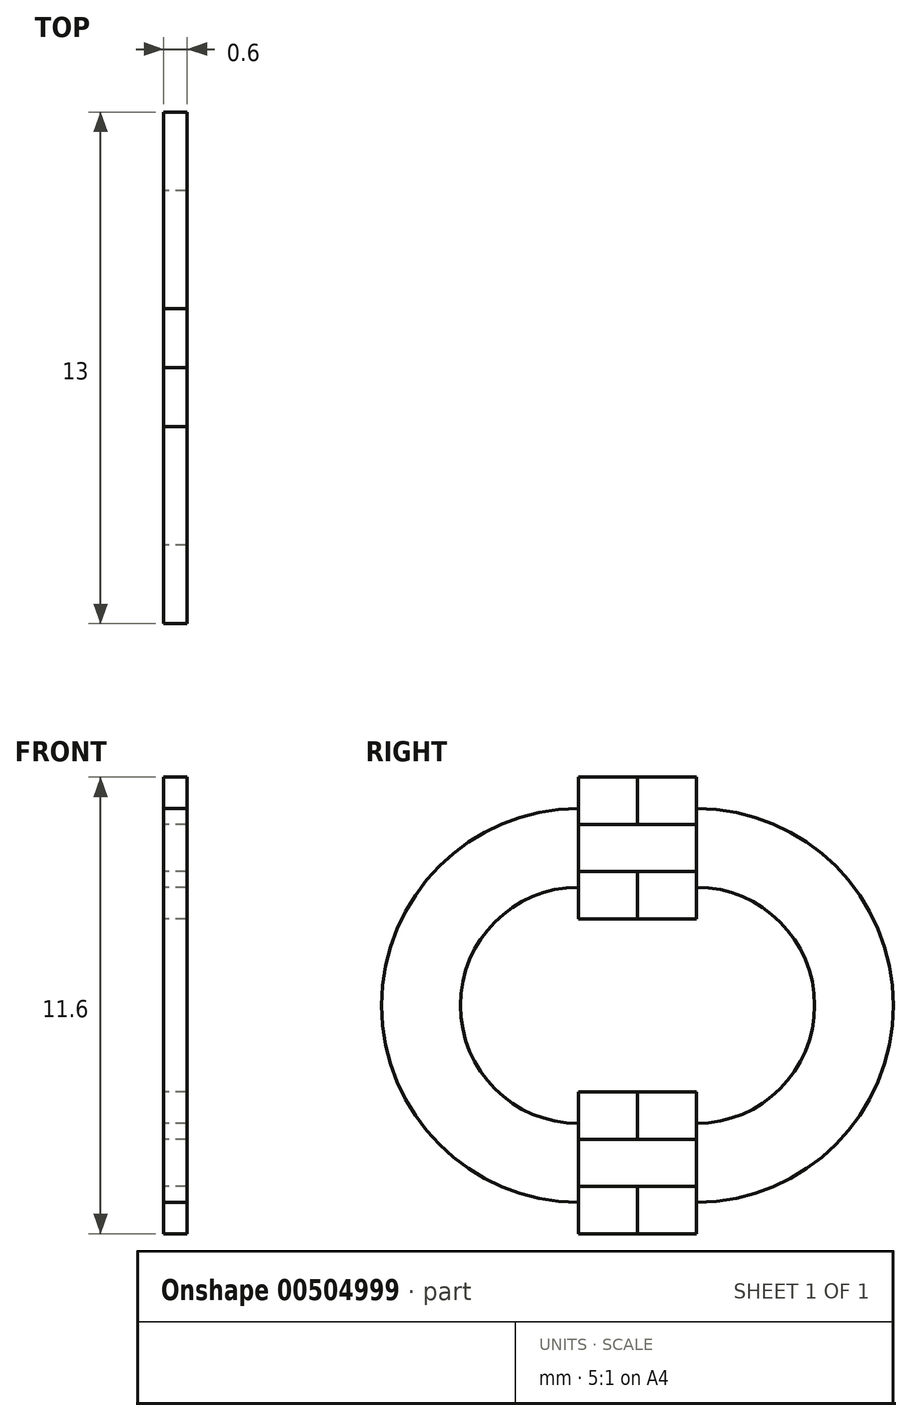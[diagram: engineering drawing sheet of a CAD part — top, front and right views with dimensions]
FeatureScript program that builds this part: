
annotation { "Feature Type Name" : "Feature", "Feature Type Description" : "" }
export const myFeature = defineFeature(function(context is Context, id is Id, definition is map)
    precondition{}
    {
        {
            var Q0;
            Q0=qCreatedBy(makeId("Right.planeOp"),FACE);
            cPlane(context, id + "F0", {"entities" : qUnion([Q0]), "cplaneType" : CPlaneType.OFFSET, "offset" : 7.5 * mm, "width" : 150 * mm, "height" : 150 * mm});
        }
        {
            var Q0;
            Q0=qCreatedBy(id+"F0.planeOp",FACE);
            var sketch = newSketch(context, id + "F1", { "sketchPlane" : qUnion([Q0])});
            skPoint(sketch, "E0.0", {"position": v(0, 0) * mm});
            skArc(sketch, "E1", {"start": v(0, -5) * mm, "mid": v(5, 0) * mm, "end": v(0, 5) * mm});
            skArc(sketch, "E2", {"start": v(0, -3) * mm, "mid": v(3, 0) * mm, "end": v(0, 3) * mm});
            skPoint(sketch, "E3.orphan", {"position": v(0, -7.41) * mm});
            skLineSegment(sketch, "E4", {"start": v(0, 5) * mm, "end": v(0, 4.6) * mm});
            skLineSegment(sketch, "E5", {"start": v(0, -3) * mm, "end": v(0, -3.4) * mm});
            skLineSegment(sketch, "E6.0", {"start": v(0, 4.6) * mm, "end": v(-1.5, 4.6) * mm});
            skLineSegment(sketch, "E7.0", {"start": v(0, 3.4) * mm, "end": v(-1.5, 3.4) * mm});
            skLineSegment(sketch, "E8", {"start": v(-3, 5.8) * mm, "end": v(-1.5, 5.8) * mm});
            skLineSegment(sketch, "E9", {"start": v(-1.5, 4.6) * mm, "end": v(-1.5, 5.8) * mm});
            skLineSegment(sketch, "E10.MirrorCS", {"start": v(-3, 2.2) * mm, "end": v(-1.5, 2.2) * mm});
            skLineSegment(sketch, "E11.trimOffspring", {"start": v(0, 3.4) * mm, "end": v(0, 3) * mm});
            skLineSegment(sketch, "E12.trimOffspring", {"start": v(-1.5, 3.4) * mm, "end": v(-1.5, 2.2) * mm});
            skLineSegment(sketch, "E13", {"start": v(0, 0) * mm, "end": v(6.92, 0) * mm, "construction": true});
            skLineSegment(sketch, "E14.trimOffspring", {"start": v(0, -4.6) * mm, "end": v(0, -5) * mm});
            skLineSegment(sketch, "E15.0", {"start": v(-3, 2.2) * mm, "end": v(-3, 5.8) * mm});
            skLineSegment(sketch, "E16.MirrorCS", {"start": v(0, -3.4) * mm, "end": v(-1.5, -3.4) * mm});
            skLineSegment(sketch, "E17.MirrorCS", {"start": v(0, -4.6) * mm, "end": v(-1.5, -4.6) * mm});
            skLineSegment(sketch, "E18.MirrorCS", {"start": v(-1.5, -4.6) * mm, "end": v(-1.5, -5.8) * mm});
            skLineSegment(sketch, "E19.MirrorCS", {"start": v(-1.5, -3.4) * mm, "end": v(-1.5, -2.2) * mm});
            skLineSegment(sketch, "E20.MirrorCS", {"start": v(-3, -5.8) * mm, "end": v(-1.5, -5.8) * mm});
            skLineSegment(sketch, "E21.MirrorCS", {"start": v(-3, -2.2) * mm, "end": v(-1.5, -2.2) * mm});
            skLineSegment(sketch, "E22.MirrorCS", {"start": v(-3, -2.2) * mm, "end": v(-3, -5.8) * mm});
            skSolve(sketch);
        }
        {
            var Q0;
            Q0=makeQuery(id+"F1.imprint","IMPRINT",FACE,{"disambiguationData":[TD([[makeQuery(id+"F1.imprint","IMPRINT",EDGE,{"derivedFrom":sQuery(id+"F1.wireOp",EDGE,"E1")}),1.0]])]});
            extrude(context, id + "F2", {"entities" : qUnion([Q0]), "depth" : 0.6 * mm});
        }
        {
            var Q0;
            Q0=qCreatedBy(makeId("Front.planeOp"),FACE);
            var Q1;
            Q1=sQuery(id+"F1.wireOp",VERTEX,"E7.0.end");
            cPlane(context, id + "F3", {"entities" : qUnion([Q0, Q1]), "cplaneType" : CPlaneType.PLANE_POINT, "offset" : 25 * mm, "width" : 150 * mm, "height" : 150 * mm});
        }
        {
            var Q0;
            Q0=makeQuery(id+"F2.opExtrude","SWEPT_BODY",BODY,{"disambiguationData":[OSD([sQuery(id+"F1.wireOp",EDGE,"E1"),sQuery(id+"F1.wireOp",EDGE,"E2"),sQuery(id+"F1.wireOp",EDGE,"E4"),sQuery(id+"F1.wireOp",EDGE,"E5"),sQuery(id+"F1.wireOp",EDGE,"E6.0"),sQuery(id+"F1.wireOp",EDGE,"E7.0"),sQuery(id+"F1.wireOp",EDGE,"E8"),sQuery(id+"F1.wireOp",EDGE,"E9"),sQuery(id+"F1.wireOp",EDGE,"E10.MirrorCS"),sQuery(id+"F1.wireOp",EDGE,"E11.trimOffspring"),sQuery(id+"F1.wireOp",EDGE,"E12.trimOffspring"),sQuery(id+"F1.wireOp",EDGE,"E14.trimOffspring"),sQuery(id+"F1.wireOp",EDGE,"E15.0"),sQuery(id+"F1.wireOp",EDGE,"E16.MirrorCS"),sQuery(id+"F1.wireOp",EDGE,"E17.MirrorCS"),sQuery(id+"F1.wireOp",EDGE,"E18.MirrorCS"),sQuery(id+"F1.wireOp",EDGE,"E19.MirrorCS"),sQuery(id+"F1.wireOp",EDGE,"E20.MirrorCS"),sQuery(id+"F1.wireOp",EDGE,"E21.MirrorCS"),sQuery(id+"F1.wireOp",EDGE,"E22.MirrorCS")])]});
            var Q1;
            Q1=qCreatedBy(id+"F3.planeOp",FACE);
            mirror(context, id + "F4", {"entities" : qUnion([Q0]), "mirrorPlane" : qUnion([Q1])});
        }
    });
